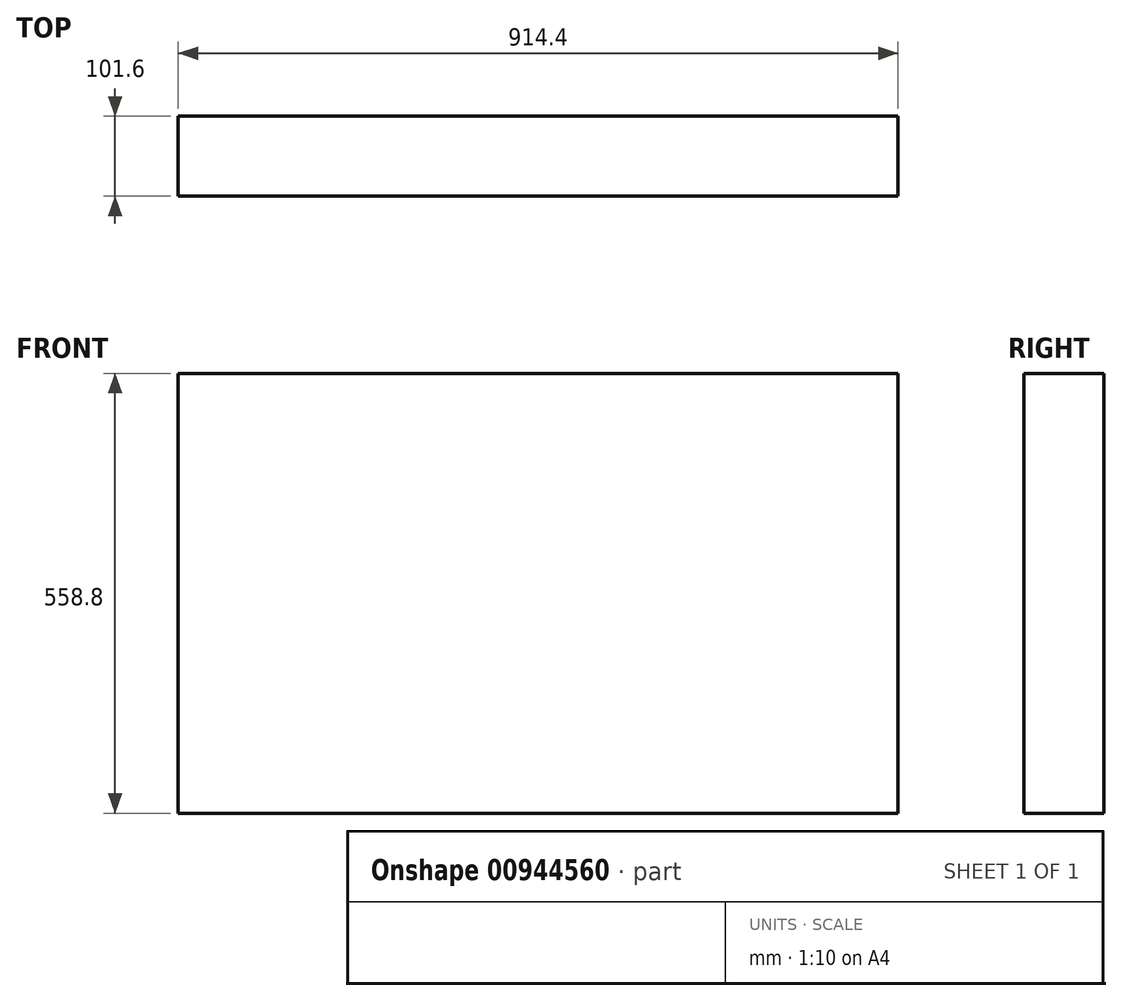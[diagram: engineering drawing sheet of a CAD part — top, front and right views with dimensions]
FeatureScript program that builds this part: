
annotation { "Feature Type Name" : "Feature", "Feature Type Description" : "" }
export const myFeature = defineFeature(function(context is Context, id is Id, definition is map)
    precondition{}
    {
        {
            var Q0;
            Q0=qCreatedBy(makeId("Front.planeOp"),FACE);
            var sketch = newSketch(context, id + "F0", { "sketchPlane" : qUnion([Q0])});
            skLineSegment(sketch, "E0.bottom", {"start": v(0, 0) * mm, "end": v(914.4, 0) * mm});
            skLineSegment(sketch, "E0.top", {"start": v(0, 558.8) * mm, "end": v(914.4, 558.8) * mm});
            skLineSegment(sketch, "E0.left", {"start": v(0, 0) * mm, "end": v(0, 558.8) * mm});
            skLineSegment(sketch, "E0.right", {"start": v(914.4, 0) * mm, "end": v(914.4, 558.8) * mm});
            skSolve(sketch);
        }
        {
            var Q0;
            Q0 = qSketchRegion(id + "F0", true);
            extrude(context, id + "F1", {"entities" : qUnion([Q0]), "depth" : 101.6 * mm, "offsetDistance" : 25.4 * mm});
        }
    });
